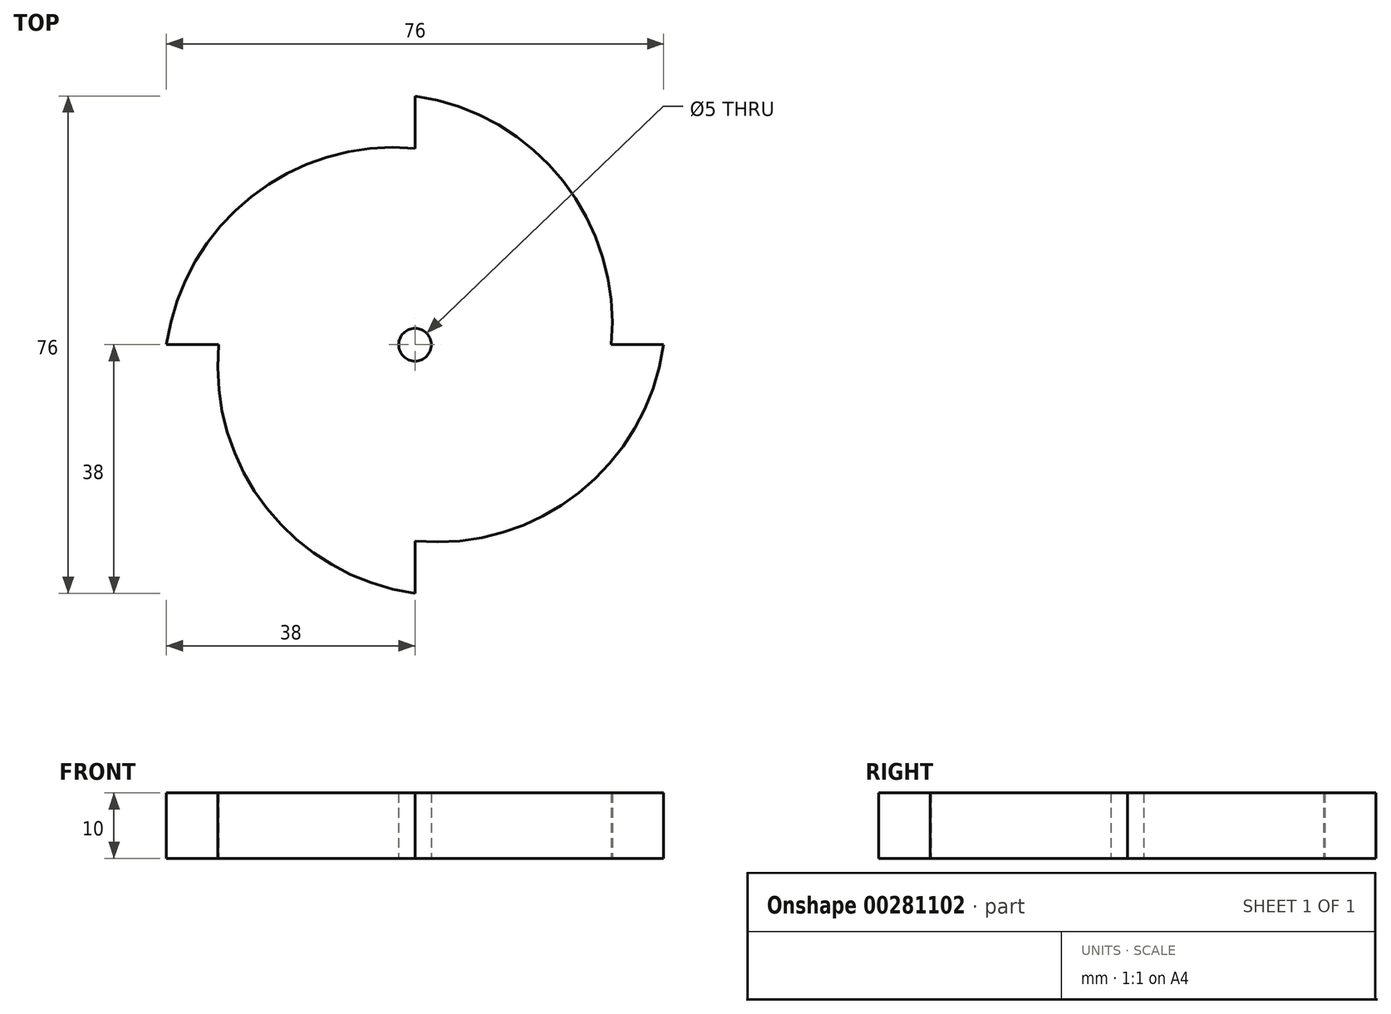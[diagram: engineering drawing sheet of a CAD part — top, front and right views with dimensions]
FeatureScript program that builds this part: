
annotation { "Feature Type Name" : "Feature", "Feature Type Description" : "" }
export const myFeature = defineFeature(function(context is Context, id is Id, definition is map)
    precondition{}
    {
        {
            var Q0;
            Q0=qCreatedBy(makeId("Top.planeOp"),FACE);
            var sketch = newSketch(context, id + "F0", { "sketchPlane" : qUnion([Q0])});
            skCircle(sketch, "E0", {"center": v(0, 0) * mm, "radius": 30 * mm});
            skLineSegment(sketch, "E1", {"start": v(0, 30) * mm, "end": v(0, 38) * mm});
            skArc(sketch, "E2", {"start": v(30, 0) * mm, "mid": v(22.63, 25.02) * mm, "end": v(0, 38) * mm});
            skLineSegment(sketch, "E3", {"start": v(30, 0) * mm, "end": v(38, 0) * mm});
            skArc(sketch, "E4", {"start": v(0, -30) * mm, "mid": v(25.02, -22.63) * mm, "end": v(38, 0) * mm});
            skLineSegment(sketch, "E5", {"start": v(0, -30) * mm, "end": v(0, -38) * mm});
            skArc(sketch, "E6", {"start": v(-30, 0) * mm, "mid": v(-22.63, -25.02) * mm, "end": v(0, -38) * mm});
            skLineSegment(sketch, "E7", {"start": v(-30, 0) * mm, "end": v(-38, 0) * mm});
            skArc(sketch, "E8", {"start": v(0, 30) * mm, "mid": v(-25.02, 22.63) * mm, "end": v(-38, 0) * mm});
            skCircle(sketch, "E9", {"center": v(0, 0) * mm, "radius": 2.5 * mm});
            skSolve(sketch);
        }
        {
            var Q0;
            Q0 = qSketchRegion(id + "F0", true);
            extrude(context, id + "F1", {"entities" : qUnion([Q0]), "depth" : 10 * mm});
        }
    });
